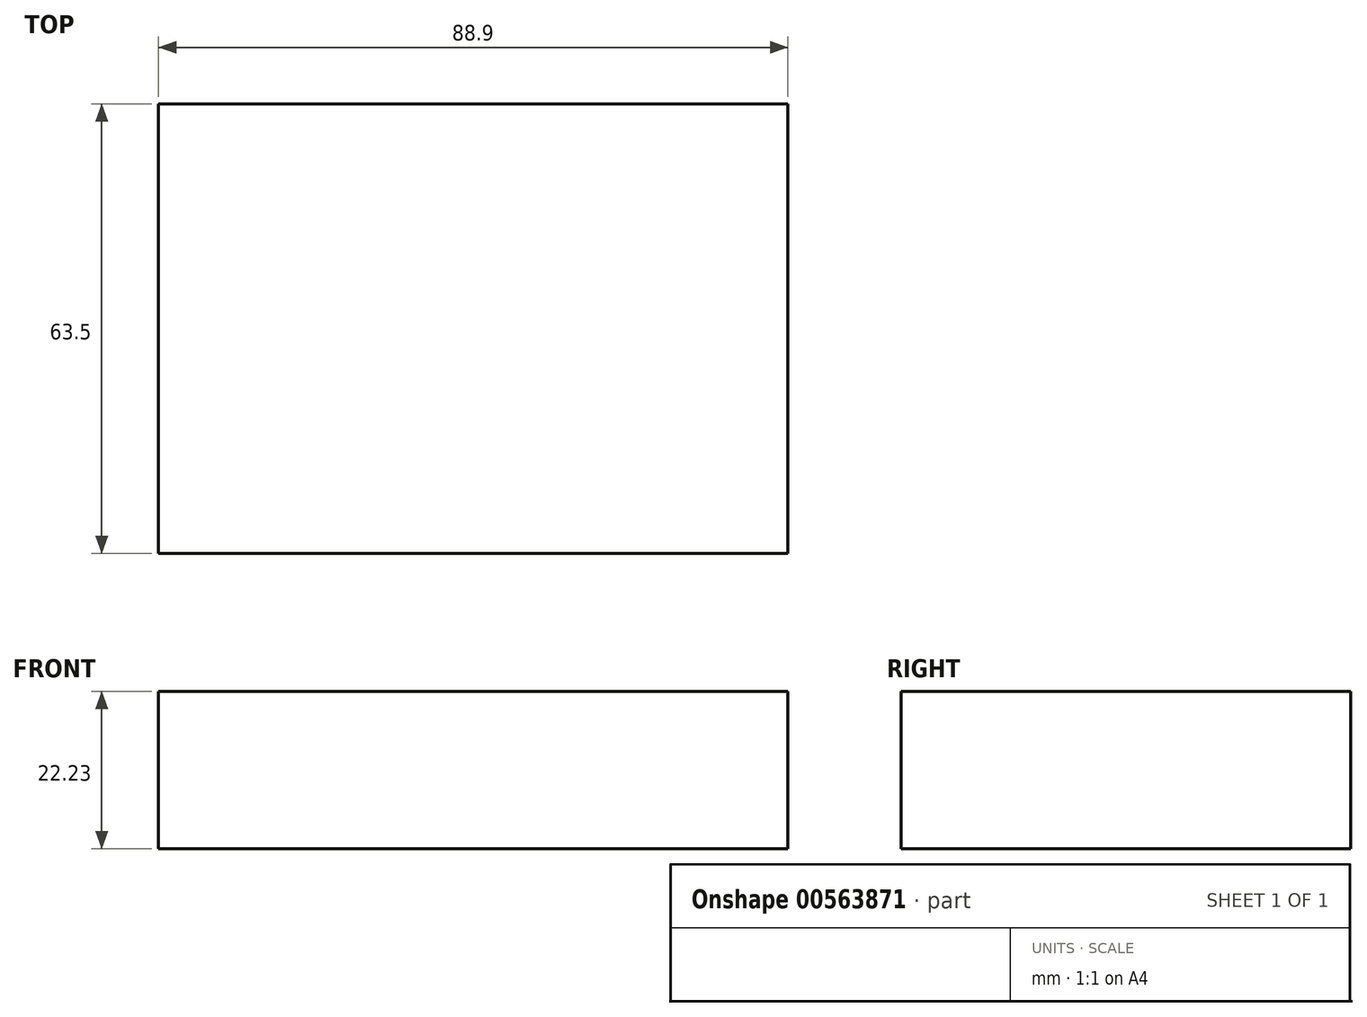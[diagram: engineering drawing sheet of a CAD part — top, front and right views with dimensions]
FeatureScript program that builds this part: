
annotation { "Feature Type Name" : "Feature", "Feature Type Description" : "" }
export const myFeature = defineFeature(function(context is Context, id is Id, definition is map)
    precondition{}
    {
        {
            var Q0;
            Q0=qCreatedBy(makeId("Top.planeOp"),FACE);
            var sketch = newSketch(context, id + "F0", { "sketchPlane" : qUnion([Q0])});
            skLineSegment(sketch, "E0.bottom", {"start": v(0, 0) * mm, "end": v(88.9, 0) * mm});
            skLineSegment(sketch, "E0.top", {"start": v(0, 63.5) * mm, "end": v(88.9, 63.5) * mm});
            skLineSegment(sketch, "E0.left", {"start": v(0, 0) * mm, "end": v(0, 63.5) * mm});
            skLineSegment(sketch, "E0.right", {"start": v(88.9, 0) * mm, "end": v(88.9, 63.5) * mm});
            skSolve(sketch);
        }
        {
            var Q0;
            Q0=makeQuery(id+"F0.imprint","IMPRINT",FACE,{"disambiguationData":[TD([[makeQuery(id+"F0.imprint","IMPRINT",EDGE,{"derivedFrom":sQuery(id+"F0.wireOp",EDGE,"E0.bottom")}),1.0]])]});
            extrude(context, id + "F1", {"entities" : qUnion([Q0]), "depth" : 22.22 * mm, "offsetDistance" : 25.4 * mm});
        }
    });
